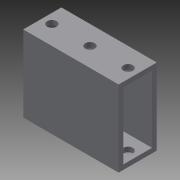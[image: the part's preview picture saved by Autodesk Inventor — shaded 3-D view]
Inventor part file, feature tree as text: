
AUTODESK INVENTOR PART (.ipt)
format: ipt  version: 2015 SP1 (Build 190203100, 203)  size: 99,328 bytes
history: native  units: in
note: dims shown in document units (in); Inventor stores cm internally (conversion verified against a paired STEP export)
features: sketch x2, extrude x1, hole x1
ambient origin geometry x8: Origin, YZ Plane, XZ Plane, XY Plane, X Axis, Y Axis, Z Axis, Center Point
bodies: Solid1 (feature_tree)
feature tree (4):
  extrude  "Extrusion1"  Depth=1.0in
  hole  "Hole1"  [1 undecoded]
  sketch  "Sketch1"  dims[d0=2.0in d1=1.0in]
  sketch  "Sketch2"  dims[d2=1.75in d3=0.75in d4=0.125in d5=0.125in d6=2.5in d7=0.0in d8=0.25in d9=1.25in d10=2.25in d11=0.5in d12=0.5in d13=0.5in d14=0.25in d15=0.75in d16=0.375in d17=0.25in d18=0.5635in d19=1.0in d20=0.8108in]
note: 1 required parameter value undecoded (feature->parameter linkage not recoverable at this tier; creation-order binding heuristic only, values carry confidence <= 0.55)
